# Revit family: Sink-Undermount-Lavatory-KOHLER-LAUREATE_CAXTON-K-14008T_1
name_source: partatom
category: Plumbing Fixtures
revit_build: Autodesk Revit 2017 (Build: 20160225_1515(x64)
units: mm (PartAtom-declared; Revit-internal decimal feet)

## family parameters
Cut with Voids When Loaded = No
Host = Face
OmniClass Number = 23.31.13.00
OmniClass Title = Sinks
Part Type = Normal
Room Calculation Point = No
Round Connector Dimension = Use Diameter
Shared = No

## types (3) — shared parameters
ADA Compliant = No
Assembly Code = D2010400
CW Connection = No
Cold Water Inlet = Cold Water Inlet
Date Modified = 07/13/2021
Default Elevation = 36"
Drain Included = No
Finish = Kohler-Vitreous_China-0-White
HW Connection = No
Height = 7 9/16"
Hot Water Inlet = Hot Water Inlet
Length = 17 1/4"
Manufacturer = KOHLER Co.
Master Format 2014 = 22 41 16
Master Format 2014 Name = Residential Lavatories and Sinks
Material = Vitreous China
Product Name = LAUREATE CAXTON
Product Page URL = https://www.kohler.com.cn
URL = http://www.kohler.com.cn
Vent Connection = No
Waste Connection = Yes
Waste Water Outlet = Waste Water Outlet
WaterSense Certified = No
Width = 21 1/8"

## per-type parameters (varying)
| type | Description | Model | Secondary Finish | Type |
| Rose Gold, 0-White | Rose Gold Under Counter Basin | K-14008T-RGD-0 | Kohler-Metal-RGD-Rose_Gold | 1 |
| Premium Gold, 0- White | Undercounter Basin Premium Gold | K-14008T-PD-0 | Kohler-Metal-PGD-Modern_Polished_Gold | 2 |
| Platinum, 0- White | Under Counter Basin Platinum | K-14008T-PK-0 | Kohler-Metal-PK-Platinum | 3 |

## geometry (parser evidence)
native form markers: Sweep x2
no freeform markers — native parametric forms only
